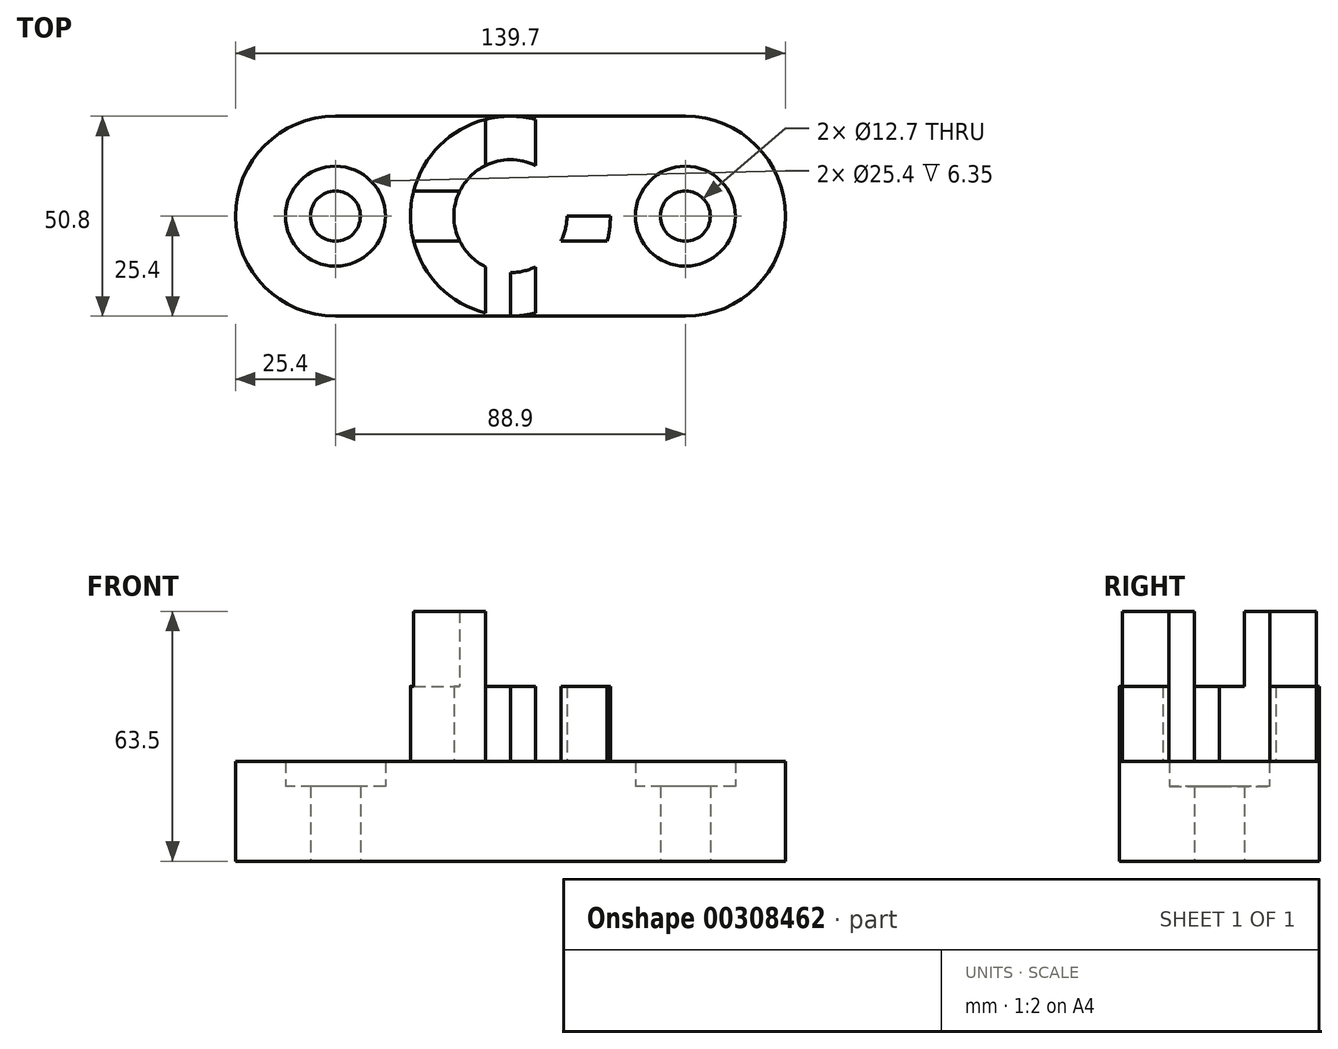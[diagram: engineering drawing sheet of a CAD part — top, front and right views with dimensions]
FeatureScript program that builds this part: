
annotation { "Feature Type Name" : "Feature", "Feature Type Description" : "" }
export const myFeature = defineFeature(function(context is Context, id is Id, definition is map)
    precondition{}
    {
        {
            var Q0;
            Q0=qCreatedBy(makeId("Top.planeOp"),FACE);
            var sketch = newSketch(context, id + "F0", { "sketchPlane" : qUnion([Q0])});
            skLineSegment(sketch, "E0", {"start": v(0, 0) * mm, "end": v(0, 12.7) * mm});
            skLineSegment(sketch, "E1", {"start": v(0, 38.1) * mm, "end": v(0, 50.8) * mm});
            skLineSegment(sketch, "E2", {"start": v(0, 50.8) * mm, "end": v(44.45, 50.8) * mm});
            skLineSegment(sketch, "E3", {"start": v(44.45, 50.8) * mm, "end": v(88.9, 50.8) * mm});
            skLineSegment(sketch, "E4", {"start": v(88.9, 50.8) * mm, "end": v(88.9, 38.1) * mm});
            skLineSegment(sketch, "E5", {"start": v(88.9, 12.7) * mm, "end": v(88.9, 0) * mm});
            skLineSegment(sketch, "E6", {"start": v(88.9, 0) * mm, "end": v(44.45, 0) * mm});
            skLineSegment(sketch, "E7", {"start": v(44.45, 0) * mm, "end": v(0, 0) * mm});
            skArc(sketch, "E8", {"start": v(0, 50.8) * mm, "mid": v(-25.4, 25.4) * mm, "end": v(0, 0) * mm});
            skArc(sketch, "E9", {"start": v(88.9, 0) * mm, "mid": v(114.3, 25.4) * mm, "end": v(88.9, 50.8) * mm});
            skCircle(sketch, "E10", {"center": v(0, 25.4) * mm, "radius": 12.7 * mm});
            skCircle(sketch, "E11", {"center": v(88.9, 25.4) * mm, "radius": 12.7 * mm});
            skCircle(sketch, "E12", {"center": v(0, 25.4) * mm, "radius": 6.35 * mm});
            skCircle(sketch, "E13", {"center": v(88.9, 25.4) * mm, "radius": 6.35 * mm});
            skSolve(sketch);
        }
        {
            var Q0;
            Q0=makeQuery(id+"F0.imprint","IMPRINT",FACE,{"disambiguationData":[TD([[makeQuery(id+"F0.imprint","IMPRINT",EDGE,{"derivedFrom":sQuery(id+"F0.wireOp",EDGE,"E12")}),-1.0]])]});
            extrude(context, id + "F1", {"entities" : qUnion([Q0]), "depth" : 19.05 * mm});
        }
        {
            var Q0;
            {var subQ4=sQuery(id+"F0.wireOp",EDGE,"E0");Q0=makeQuery(id+"F0.imprint","IMPRINT",FACE,{"disambiguationData":[TD([[makeQuery(id+"F0.imprint","IMPRINT",EDGE,{"derivedFrom":subQ4}),-1.0]])]});}
            var Q1;
            {var subQ0=sQuery(id+"F0.wireOp",EDGE,"E0");Q1=makeQuery(id+"F0.imprint","IMPRINT",FACE,{"disambiguationData":[TD([[makeQuery(id+"F0.imprint","IMPRINT",EDGE,{"derivedFrom":subQ0}),1.0]])]});}
            extrude(context, id + "F2", {"entities" : qUnion([Q0, Q1]), "operationType" : NewBodyOperationType.ADD, "depth" : 25.4 * mm});
        }
        {
            var Q0;
            Q0=makeQuery(id+"F0.imprint","IMPRINT",FACE,{"disambiguationData":[TD([[makeQuery(id+"F0.imprint","IMPRINT",EDGE,{"derivedFrom":sQuery(id+"F0.wireOp",EDGE,"E13")}),-1.0]])]});
            extrude(context, id + "F3", {"entities" : qUnion([Q0]), "operationType" : NewBodyOperationType.ADD, "depth" : 19.05 * mm});
        }
        {
            var Q0;
            {var subQ0=sQuery(id+"F0.wireOp",EDGE,"E4");Q0=makeQuery(id+"F0.imprint","IMPRINT",FACE,{"disambiguationData":[TD([[makeQuery(id+"F0.imprint","IMPRINT",EDGE,{"derivedFrom":subQ0}),1.0]])]});}
            extrude(context, id + "F4", {"entities" : qUnion([Q0]), "operationType" : NewBodyOperationType.ADD, "depth" : 25.4 * mm});
        }
        {
            var Q0;
            {var subQ0=sQuery(id+"F0.wireOp",EDGE,"E11");var subQ1=sQuery(id+"F0.wireOp",EDGE,"E5");var subQ2=sQuery(id+"F0.wireOp",EDGE,"E4");Q0=makeQuery(id+"F4.boolean.opBoolean","MERGE",FACE,{"derivedFrom":[makeQuery(id+"F2.opExtrude","CAP_FACE",FACE,{"disambiguationData":[OSD([sQuery(id+"F0.wireOp",EDGE,"E2"),sQuery(id+"F0.wireOp",EDGE,"E3"),subQ2,subQ1,sQuery(id+"F0.wireOp",EDGE,"E6"),sQuery(id+"F0.wireOp",EDGE,"E7"),sQuery(id+"F0.wireOp",EDGE,"E8"),sQuery(id+"F0.wireOp",EDGE,"E10"),subQ0])],"isStart":false}),makeQuery(id+"F4.opExtrude","CAP_FACE",FACE,{"disambiguationData":[OSD([subQ2,subQ1,sQuery(id+"F0.wireOp",EDGE,"E9"),subQ0])],"isStart":false})]});}
            var sketch = newSketch(context, id + "F5", { "sketchPlane" : qUnion([Q0])});
            skCircle(sketch, "E14", {"center": v(44.45, 25.4) * mm, "radius": 25.4 * mm});
            skPoint(sketch, "E14.centerSnap0", {"position": v(114.3, 25.4) * mm});
            skPoint(sketch, "E14.centerSnap1", {"position": v(44.45, 0) * mm});
            skCircle(sketch, "E15", {"center": v(44.45, 25.4) * mm, "radius": 14.35 * mm});
            skLineSegment(sketch, "E16", {"start": v(44.45, 25.4) * mm, "end": v(19.05, 25.4) * mm});
            skLineSegment(sketch, "E17", {"start": v(19.05, 25.4) * mm, "end": v(19.05, 31.75) * mm});
            skLineSegment(sketch, "E18", {"start": v(19.05, 31.75) * mm, "end": v(71.1, 31.75) * mm});
            skLineSegment(sketch, "E19", {"start": v(71.1, 31.75) * mm, "end": v(71.1, 25.4) * mm});
            skLineSegment(sketch, "E20", {"start": v(71.1, 25.4) * mm, "end": v(44.45, 25.4) * mm});
            skLineSegment(sketch, "E21", {"start": v(19.05, 25.4) * mm, "end": v(19.05, 19.05) * mm});
            skLineSegment(sketch, "E22", {"start": v(19.05, 19.05) * mm, "end": v(71.1, 19.05) * mm});
            skLineSegment(sketch, "E23", {"start": v(71.1, 19.05) * mm, "end": v(71.1, 25.4) * mm});
            skLineSegment(sketch, "E24", {"start": v(44.45, 25.4) * mm, "end": v(44.45, 50.8) * mm});
            skLineSegment(sketch, "E25", {"start": v(44.45, 50.8) * mm, "end": v(38.1, 50.8) * mm});
            skLineSegment(sketch, "E26", {"start": v(38.1, 50.8) * mm, "end": v(38.1, 0) * mm});
            skLineSegment(sketch, "E27", {"start": v(38.1, 0) * mm, "end": v(44.45, 0) * mm});
            skLineSegment(sketch, "E28", {"start": v(50.8, 0) * mm, "end": v(50.8, 50.8) * mm});
            skLineSegment(sketch, "E29", {"start": v(50.8, 50.8) * mm, "end": v(44.45, 50.8) * mm});
            skLineSegment(sketch, "E30", {"start": v(44.45, 0) * mm, "end": v(44.45, 25.4) * mm});
            skSolve(sketch);
        }
        {
            var Q0;
            {var subQ0=sQuery(id+"F5.wireOp",EDGE,"E26");var subQ1=sQuery(id+"F5.wireOp",EDGE,"E14");var subQ2=makeQuery(id+"F5.imprint","INTERSECT",VERTEX,{"disambiguationData":[OD(0.0)],"derivedFrom":[subQ1,subQ0]});Q0=makeQuery(id+"F5.imprint","IMPRINT",FACE,{"disambiguationData":[TD([[makeQuery(id+"F5.imprint","IMPRINT",EDGE,{"disambiguationData":[TD([[subQ2,-1.0]])],"derivedFrom":subQ1}),1.0]])]});}
            var Q1;
            {var subQ0=sQuery(id+"F5.wireOp",EDGE,"E24");var subQ5=sQuery(id+"F5.wireOp",EDGE,"E15");var subQ6=makeQuery(id+"F5.imprint","INTERSECT",VERTEX,{"derivedFrom":[subQ5,subQ0]});Q1=makeQuery(id+"F5.imprint","IMPRINT",FACE,{"disambiguationData":[TD([[makeQuery(id+"F5.imprint","IMPRINT",EDGE,{"disambiguationData":[TD([[subQ6,-1.0]])],"derivedFrom":subQ5}),-1.0]])]});}
            var Q2;
            {var subQ3=sQuery(id+"F5.wireOp",EDGE,"E28");var subQ5=sQuery(id+"F5.wireOp",EDGE,"E15");var subQ6=makeQuery(id+"F5.imprint","INTERSECT",VERTEX,{"disambiguationData":[OD(0.0)],"derivedFrom":[subQ5,subQ3]});Q2=makeQuery(id+"F5.imprint","IMPRINT",FACE,{"disambiguationData":[TD([[makeQuery(id+"F5.imprint","IMPRINT",EDGE,{"disambiguationData":[TD([[subQ6,-1.0]])],"derivedFrom":subQ5}),-1.0]])]});}
            var Q3;
            {var subQ0=sQuery(id+"F5.wireOp",EDGE,"E18");var subQ1=sQuery(id+"F5.wireOp",EDGE,"E14");var subQ2=makeQuery(id+"F5.imprint","INTERSECT",VERTEX,{"disambiguationData":[OD(0.0)],"derivedFrom":[subQ1,subQ0]});Q3=makeQuery(id+"F5.imprint","IMPRINT",FACE,{"disambiguationData":[TD([[makeQuery(id+"F5.imprint","IMPRINT",EDGE,{"disambiguationData":[TD([[subQ2,-1.0]])],"derivedFrom":subQ1}),1.0]])]});}
            var Q4;
            {var subQ0=sQuery(id+"F5.wireOp",EDGE,"E18");var subQ1=sQuery(id+"F5.wireOp",EDGE,"E14");var subQ2=makeQuery(id+"F5.imprint","INTERSECT",VERTEX,{"disambiguationData":[OD(0.0)],"derivedFrom":[subQ1,subQ0]});Q4=makeQuery(id+"F5.imprint","IMPRINT",FACE,{"disambiguationData":[TD([[makeQuery(id+"F5.imprint","IMPRINT",EDGE,{"disambiguationData":[TD([[subQ2,1.0]])],"derivedFrom":subQ1}),1.0]])]});}
            var Q5;
            {var subQ0=sQuery(id+"F5.wireOp",EDGE,"E20");var subQ1=sQuery(id+"F5.wireOp",EDGE,"E14");var subQ2=makeQuery(id+"F5.imprint","INTERSECT",VERTEX,{"derivedFrom":[subQ1,subQ0]});Q5=makeQuery(id+"F5.imprint","IMPRINT",FACE,{"disambiguationData":[TD([[makeQuery(id+"F5.imprint","IMPRINT",EDGE,{"disambiguationData":[TD([[subQ2,1.0]])],"derivedFrom":subQ1}),1.0]])]});}
            var Q6;
            {var subQ0=sQuery(id+"F5.wireOp",EDGE,"E28");var subQ1=sQuery(id+"F5.wireOp",EDGE,"E14");var subQ2=makeQuery(id+"F5.imprint","INTERSECT",VERTEX,{"disambiguationData":[OD(1.0)],"derivedFrom":[subQ1,subQ0]});Q6=makeQuery(id+"F5.imprint","IMPRINT",FACE,{"disambiguationData":[TD([[makeQuery(id+"F5.imprint","IMPRINT",EDGE,{"disambiguationData":[TD([[subQ2,-1.0]])],"derivedFrom":subQ1}),1.0]])]});}
            var Q7;
            {var subQ0=sQuery(id+"F5.wireOp",EDGE,"E30");var subQ5=sQuery(id+"F5.wireOp",EDGE,"E15");var subQ6=makeQuery(id+"F5.imprint","INTERSECT",VERTEX,{"derivedFrom":[subQ5,subQ0]});Q7=makeQuery(id+"F5.imprint","IMPRINT",FACE,{"disambiguationData":[TD([[makeQuery(id+"F5.imprint","IMPRINT",EDGE,{"disambiguationData":[TD([[subQ6,-1.0]])],"derivedFrom":subQ5}),-1.0]])]});}
            var Q8;
            {var subQ3=sQuery(id+"F5.wireOp",EDGE,"E26");var subQ5=sQuery(id+"F5.wireOp",EDGE,"E15");var subQ7=makeQuery(id+"F5.imprint","INTERSECT",VERTEX,{"disambiguationData":[OD(1.0)],"derivedFrom":[subQ5,subQ3]});Q8=makeQuery(id+"F5.imprint","IMPRINT",FACE,{"disambiguationData":[TD([[makeQuery(id+"F5.imprint","IMPRINT",EDGE,{"disambiguationData":[TD([[subQ7,-1.0]])],"derivedFrom":subQ5}),-1.0]])]});}
            var Q9;
            {var subQ0=sQuery(id+"F5.wireOp",EDGE,"E22");var subQ1=sQuery(id+"F5.wireOp",EDGE,"E14");var subQ2=makeQuery(id+"F5.imprint","INTERSECT",VERTEX,{"disambiguationData":[OD(0.0)],"derivedFrom":[subQ1,subQ0]});Q9=makeQuery(id+"F5.imprint","IMPRINT",FACE,{"disambiguationData":[TD([[makeQuery(id+"F5.imprint","IMPRINT",EDGE,{"disambiguationData":[TD([[subQ2,-1.0]])],"derivedFrom":subQ1}),1.0]])]});}
            var Q10;
            {var subQ0=sQuery(id+"F5.wireOp",EDGE,"E16");var subQ5=sQuery(id+"F5.wireOp",EDGE,"E15");var subQ6=makeQuery(id+"F5.imprint","INTERSECT",VERTEX,{"derivedFrom":[subQ5,subQ0]});Q10=makeQuery(id+"F5.imprint","IMPRINT",FACE,{"disambiguationData":[TD([[makeQuery(id+"F5.imprint","IMPRINT",EDGE,{"disambiguationData":[TD([[subQ6,-1.0]])],"derivedFrom":subQ5}),-1.0]])]});}
            var Q11;
            {var subQ3=sQuery(id+"F5.wireOp",EDGE,"E18");var subQ5=sQuery(id+"F5.wireOp",EDGE,"E15");var subQ6=makeQuery(id+"F5.imprint","INTERSECT",VERTEX,{"disambiguationData":[OD(1.0)],"derivedFrom":[subQ5,subQ3]});Q11=makeQuery(id+"F5.imprint","IMPRINT",FACE,{"disambiguationData":[TD([[makeQuery(id+"F5.imprint","IMPRINT",EDGE,{"disambiguationData":[TD([[subQ6,-1.0]])],"derivedFrom":subQ5}),-1.0]])]});}
            extrude(context, id + "F6", {"entities" : qUnion([Q0, Q1, Q2, Q3, Q4, Q5, Q6, Q7, Q8, Q9, Q10, Q11]), "operationType" : NewBodyOperationType.ADD, "depth" : 38.1 * mm});
        }
        {
            var Q0;
            Q0=makeQuery(id+"F6.opExtrude","CAP_FACE",FACE,{"disambiguationData":[OSD([sQuery(id+"F5.wireOp",EDGE,"E14"),sQuery(id+"F5.wireOp",EDGE,"E15")])],"isStart":false});
            var sketch = newSketch(context, id + "F7", { "sketchPlane" : qUnion([Q0])});
            skLineSegment(sketch, "E31", {"start": v(38.1, 50.8) * mm, "end": v(50.8, 50.8) * mm});
            skLineSegment(sketch, "E32", {"start": v(50.8, 50.8) * mm, "end": v(50.8, 0) * mm});
            skLineSegment(sketch, "E33", {"start": v(50.8, 0) * mm, "end": v(38.1, 0) * mm});
            skLineSegment(sketch, "E34", {"start": v(38.1, 0) * mm, "end": v(38.1, 50.8) * mm});
            skPoint(sketch, "E35.orphan", {"position": v(34.52, 50.8) * mm});
            skLineSegment(sketch, "E36", {"start": v(19.05, 31.75) * mm, "end": v(71.1, 31.75) * mm});
            skLineSegment(sketch, "E37", {"start": v(71.1, 31.75) * mm, "end": v(71.1, 19.05) * mm});
            skLineSegment(sketch, "E38", {"start": v(71.1, 19.05) * mm, "end": v(19.05, 19.05) * mm});
            skLineSegment(sketch, "E39", {"start": v(19.05, 19.05) * mm, "end": v(19.05, 31.75) * mm});
            skSolve(sketch);
        }
        {
            var Q0;
            Q0 = qSketchRegion(id + "F7", true);
            extrude(context, id + "F8", {"entities" : qUnion([Q0]), "operationType" : NewBodyOperationType.REMOVE, "oppositeDirection" : true, "depth" : 19.05 * mm});
        }
    });
